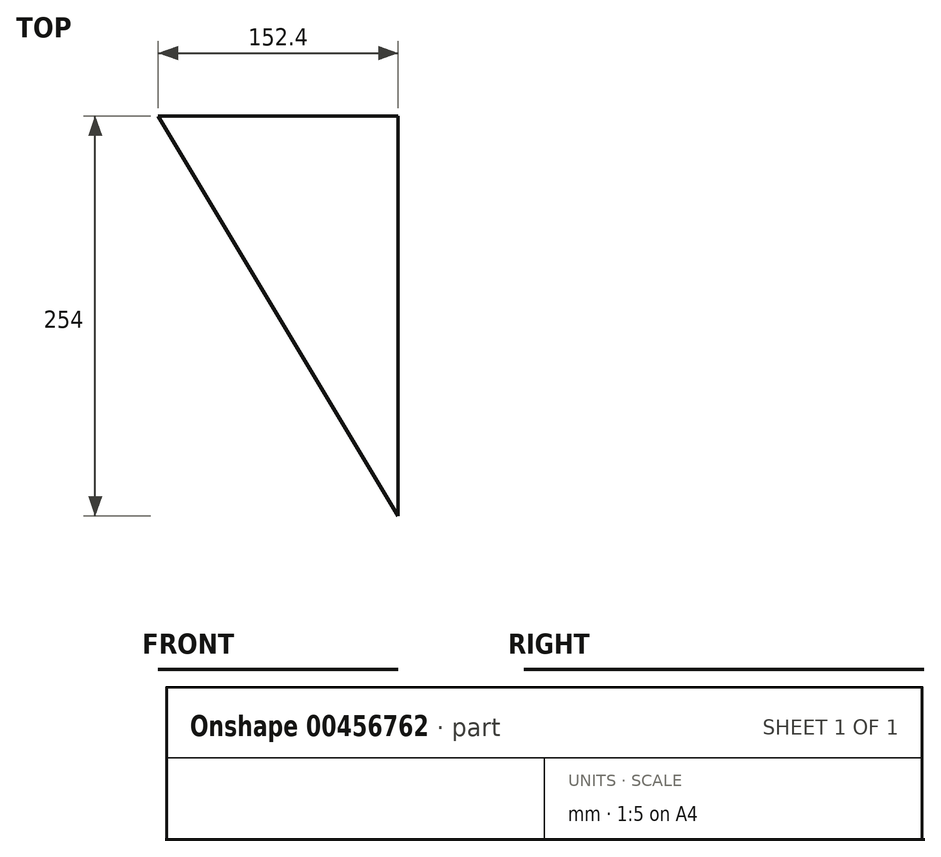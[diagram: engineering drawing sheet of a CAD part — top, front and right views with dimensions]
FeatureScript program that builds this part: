
annotation { "Feature Type Name" : "Feature", "Feature Type Description" : "" }
export const myFeature = defineFeature(function(context is Context, id is Id, definition is map)
    precondition{}
    {
        {
            var Q0;
            Q0=qCreatedBy(makeId("Top.planeOp"),FACE);
            var sketch = newSketch(context, id + "F0", { "sketchPlane" : qUnion([Q0])});
            skLineSegment(sketch, "E0", {"start": v(0, 0) * mm, "end": v(0, -254) * mm});
            skLineSegment(sketch, "E1", {"start": v(0, -254) * mm, "end": v(-152.4, 0) * mm});
            skLineSegment(sketch, "E2", {"start": v(-152.4, 0) * mm, "end": v(0, 0) * mm});
            skSolve(sketch);
        }
        {
            var Q0;
            Q0=makeQuery(id+"F0.imprint","IMPRINT",FACE,{"disambiguationData":[TD([[makeQuery(id+"F0.imprint","IMPRINT",EDGE,{"derivedFrom":sQuery(id+"F0.wireOp",EDGE,"E0")}),-1.0]])]});
            extrude(context, id + "F1", {"entities" : qUnion([Q0]), "depth" : 1 / 203.2 * mm});
        }
    });
